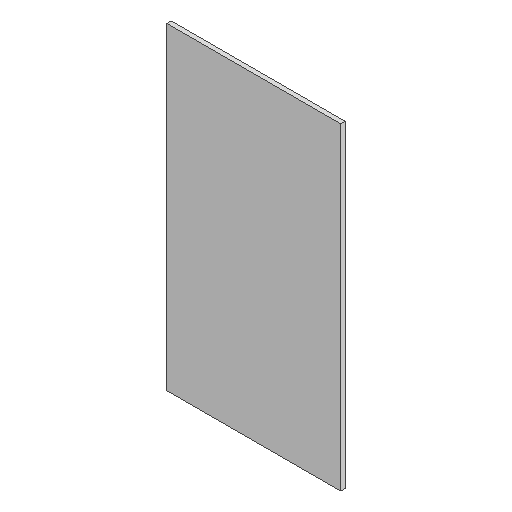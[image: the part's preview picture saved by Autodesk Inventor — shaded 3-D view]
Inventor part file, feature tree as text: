
AUTODESK INVENTOR PART (.ipt)
format: ipt  version: 2024 (Build 280153000, 153)  size: 78,848 bytes
history: native  units: mm
features: other x3, sketch x1
ambient origin geometry x8: Origin, YZ Plane, XZ Plane, XY Plane, X Axis, Y Axis, Z Axis, Center Point
bodies: Solid1 (feature_tree)
feature tree (4):
  other  "testpanel.ipt"
  other  "Solid1::testpanel.ipt"
  other  "TaggingFeature1"
  sketch  "Sketch1"  dims[d0=10.0mm]
